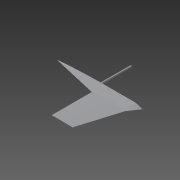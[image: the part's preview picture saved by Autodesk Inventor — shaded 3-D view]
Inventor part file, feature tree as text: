
AUTODESK INVENTOR PART (.ipt)
format: ipt  version: 2014 SP1 (Build 180222100, 222)  size: 186,880 bytes
history: native  units: mm
features: sketch x4, plane x3, loft x2, fillet x1, extrude x1, other x1
ambient origin geometry x8: Origin, YZ Plane, XZ Plane, XY Plane, X Axis, Y Axis, Z Axis, Center Point
bodies: Solid1 (feature_tree)
feature tree (12):
  sketch  "Sketch1"  dims[d0=490.0mm d11=60.0mm]
  plane  "Work Plane1"
  sketch  "Sketch2"  dims[d12=230.0mm d13=120.0mm d14=0.0mm d15=90.0deg]
  plane  "Work Plane2"
  loft  "Loft1"
  loft  "Loft2"
  plane  "Work Plane3"
  fillet  "Fillet1"  [1 undecoded]
  extrude  "Extrusion3"  TaperAngle=0.0deg  [1 undecoded]
  sketch  "Sketch3"  dims[d16=0.0mm d17=90.0deg d18=0.0mm d19=90.0deg]
  other  "Edges1"
  sketch  "Sketch5"  dims[d20=0.0mm d21=90.0deg d22=0.0mm d30=40.0mm d31=10.0mm d32=180.0mm d33=0.0mm]
note: 2 required parameter values undecoded (feature->parameter linkage not recoverable at this tier; creation-order binding heuristic only, values carry confidence <= 0.55)
